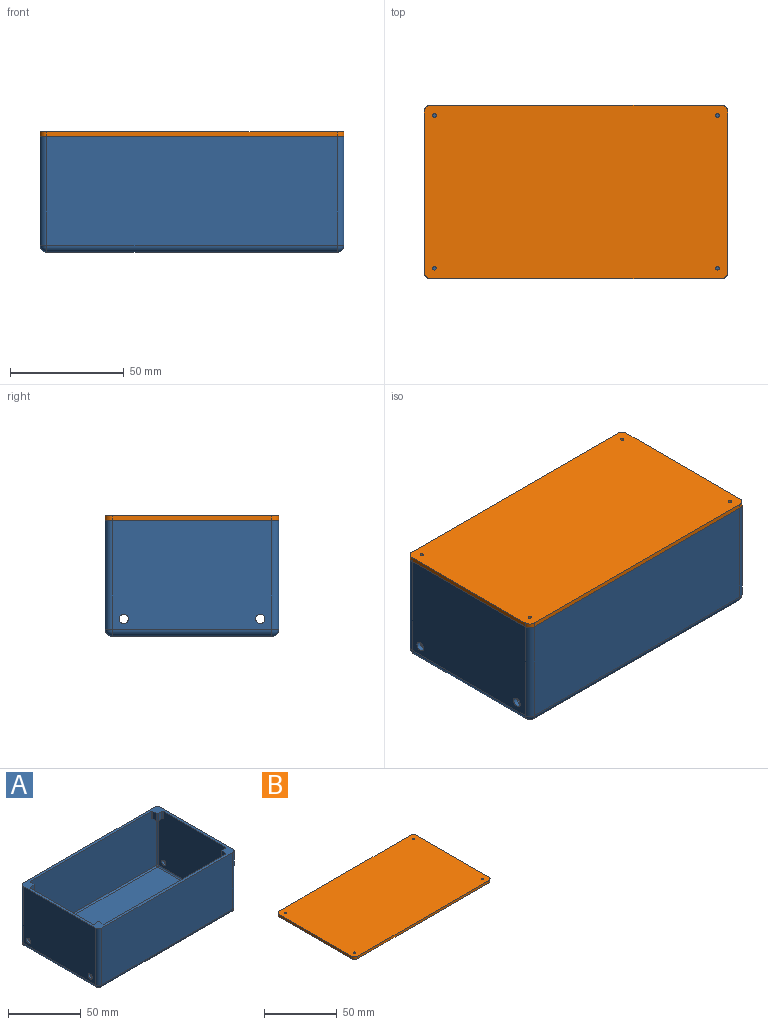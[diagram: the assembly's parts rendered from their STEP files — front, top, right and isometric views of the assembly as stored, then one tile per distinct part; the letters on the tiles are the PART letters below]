
ASSEMBLY  parts=2 mates=1
PART A: 63 faces, bbox 133.4x76.2x50.8 mm
  f0: plane 70.1x47.75mm, normal (1,0,0), area 3260.4mm2, adj f4,f23,f27,f33,f43,f46,f49,f50
  f1: plane 127.25x47.75mm, normal (0,1,0), area 6015.3mm2, adj f4,f24,f27,f29,f37,f46,f56,f62
  f2: plane 127.25x47.75mm, normal (0,-1,0), area 6015.3mm2, adj f4,f25,f31,f33,f40,f43,f58,f60
  f3: plane 70.1x47.75mm, normal (-1,0,0), area 3260.4mm2, adj f4,f26,f29,f31,f37,f40,f47,f48
  f4: plane 133.35x76.2mm, normal (0,0,1), area 930.8mm2, adj f0,f1,f2,f3,f5,f6,f7,f8
  f5: plane 70.1x47.75mm, normal (-1,0,0), area 3321.7mm2, adj f4,f10,f14,f20,f49,f50
  f6: plane 127.25x47.75mm, normal (0,-1,0), area 6076.6mm2, adj f4,f11,f14,f16
  f7: plane 70.1x47.75mm, normal (1,0,0), area 3321.7mm2, adj f4,f13,f16,f18,f47,f48
  f8: plane 127.25x47.75mm, normal (0,1,0), area 6076.6mm2, adj f4,f12,f18,f20
  f9: plane 127.25x70.1mm, normal (0,0,-1), area 8921mm2, adj f10,f11,f12,f13
  f10: cylinder r=3.05mm len=70.1mm, axis (0,-1,0), area 335.6mm2, adj f5,f9,f15,f21
  f11: cylinder r=3.05mm len=127.25mm, axis (1,0,0), area 609.3mm2, adj f6,f9,f15,f17
  f12: cylinder r=3.05mm len=127.25mm, axis (-1,0,0), area 609.3mm2, adj f8,f9,f19,f21
  f13: cylinder r=3.05mm len=70.1mm, axis (0,1,0), area 335.6mm2, adj f7,f9,f17,f19
  f14: cylinder r=3.05mm len=47.75mm, axis (0,0,1), area 228.6mm2, adj f4,f5,f6,f15
  f15: sphere r=3.05mm, area 14.6mm2, adj f10,f11,f14
  f16: cylinder r=3.05mm len=47.75mm, axis (0,0,-1), area 228.6mm2, adj f4,f6,f7,f17
  f17: sphere r=3.05mm, area 14.6mm2, adj f11,f13,f16
  f18: cylinder r=3.05mm len=47.75mm, axis (0,0,1), area 228.6mm2, adj f4,f7,f8,f19
  f19: sphere r=3.05mm, area 14.6mm2, adj f12,f13,f18
  f20: cylinder r=3.05mm len=47.75mm, axis (0,0,-1), area 228.6mm2, adj f4,f5,f8,f21
  f21: sphere r=3.05mm, area 14.6mm2, adj f10,f12,f20
  f22: plane 127.25x70.1mm, normal (0,0,1), area 8921mm2, adj f23,f24,f25,f26
  f23: cylinder r=1.02mm len=70.1mm, axis (0,-1,0), area 111.9mm2, adj f0,f22,f28,f34
  f24: cylinder r=1.02mm len=127.25mm, axis (1,0,0), area 203.1mm2, adj f1,f22,f28,f30
  f25: cylinder r=1.02mm len=127.25mm, axis (-1,0,0), area 203.1mm2, adj f2,f22,f32,f34
  f26: cylinder r=1.02mm len=70.1mm, axis (0,1,0), area 111.9mm2, adj f3,f22,f30,f32
  f27: cylinder r=1.02mm len=41.4mm, axis (0,0,1), area 66.1mm2, adj f0,f1,f28,f46
  f28: sphere r=1.02mm, area 1.6mm2, adj f23,f24,f27
  f29: cylinder r=1.02mm len=41.4mm, axis (0,0,-1), area 66.1mm2, adj f1,f3,f30,f37
  f30: sphere r=1.02mm, area 1.6mm2, adj f24,f26,f29
  f31: cylinder r=1.02mm len=41.4mm, axis (0,0,1), area 66.1mm2, adj f2,f3,f32,f40
  f32: sphere r=1.02mm, area 1.6mm2, adj f25,f26,f31
  f33: cylinder r=1.02mm len=41.4mm, axis (0,0,-1), area 66.1mm2, adj f0,f2,f34,f43
  f34: sphere r=1.02mm, area 1.6mm2, adj f23,f25,f33
  f35: plane 6.35x3.56mm, normal (0,1,0), area 22.6mm2, adj f4,f37,f54,f61
  f36: plane 6.35x3.56mm, normal (-1,0,0), area 22.6mm2, adj f4,f37,f54,f62
  f37: plane 5.84x5.84mm, normal (0,0,-1), area 25.7mm2, adj f1,f3,f29,f35,f36,f54,f61,f62
  f38: plane 6.35x3.56mm, normal (-1,0,0), area 22.6mm2, adj f4,f40,f53,f60
  f39: plane 6.35x3.56mm, normal (0,-1,0), area 22.6mm2, adj f4,f40,f53,f59
  f40: plane 5.84x5.84mm, normal (0,0,-1), area 25.7mm2, adj f2,f3,f31,f38,f39,f53,f59,f60
  f41: plane 6.35x3.56mm, normal (0,-1,0), area 22.6mm2, adj f4,f43,f52,f57
  f42: plane 6.35x3.56mm, normal (1,0,0), area 22.6mm2, adj f4,f43,f52,f58
  f43: plane 5.84x5.84mm, normal (0,0,-1), area 25.7mm2, adj f0,f2,f33,f41,f42,f52,f57,f58
  f44: plane 6.35x3.56mm, normal (1,0,0), area 22.6mm2, adj f4,f46,f51,f56
  f45: plane 6.35x3.56mm, normal (0,1,0), area 22.6mm2, adj f4,f46,f51,f55
  f46: plane 5.84x5.84mm, normal (0,0,-1), area 25.7mm2, adj f0,f1,f27,f44,f45,f51,f55,f56
  f47: cylinder r=2.03mm len=4.06mm, axis (-1,0,0), area 25.9mm2, adj f3,f7
  f48: cylinder r=2.03mm len=4.06mm, axis (-1,0,0), area 25.9mm2, adj f3,f7
  f49: cylinder r=2.03mm len=4.06mm, axis (-1,0,0), area 25.9mm2, adj f0,f5
  f50: cylinder r=2.03mm len=4.06mm, axis (-1,0,0), area 25.9mm2, adj f0,f5
  f51: cylinder r=0.76mm len=6.35mm, axis (0,0,-1), area 7.6mm2, adj f4,f44,f45,f46
  f52: cylinder r=0.76mm len=6.35mm, axis (0,0,-1), area 7.6mm2, adj f4,f41,f42,f43
  f53: cylinder r=0.76mm len=6.35mm, axis (0,0,-1), area 7.6mm2, adj f4,f38,f39,f40
  f54: cylinder r=0.76mm len=6.35mm, axis (0,0,-1), area 7.6mm2, adj f4,f35,f36,f37
  f55: cylinder r=0.76mm len=6.35mm, axis (0,0,1), area 7.6mm2, adj f0,f4,f45,f46
  f56: cylinder r=0.76mm len=6.35mm, axis (0,0,1), area 7.6mm2, adj f1,f4,f44,f46
  f57: cylinder r=0.76mm len=6.35mm, axis (0,0,-1), area 7.6mm2, adj f0,f4,f41,f43
  f58: cylinder r=0.76mm len=6.35mm, axis (0,0,1), area 7.6mm2, adj f2,f4,f42,f43
  f59: cylinder r=0.76mm len=6.35mm, axis (0,0,-1), area 7.6mm2, adj f3,f4,f39,f40
  f60: cylinder r=0.76mm len=6.35mm, axis (0,0,-1), area 7.6mm2, adj f2,f4,f38,f40
  f61: cylinder r=0.76mm len=6.35mm, axis (0,0,1), area 7.6mm2, adj f3,f4,f35,f37
  f62: cylinder r=0.76mm len=6.35mm, axis (0,0,-1), area 7.6mm2, adj f1,f4,f36,f37
PART B: 14 faces, bbox 133.4x76.2x2 mm
  f0: plane 70.1x2.03mm, normal (-1,0,0), area 142.5mm2, adj f4,f5,f6,f9
  f1: plane 127.25x2.03mm, normal (0,-1,0), area 258.6mm2, adj f4,f5,f6,f7
  f2: plane 70.1x2.03mm, normal (1,0,0), area 142.5mm2, adj f4,f5,f7,f8
  f3: plane 127.25x2.03mm, normal (0,1,0), area 258.6mm2, adj f4,f5,f8,f9
  f4: plane 133.35x76.2mm, normal (0,0,1), area 10146mm2, adj f0,f1,f2,f3,f6,f7,f8,f9
  f5: plane 133.35x76.2mm, normal (0,0,-1), area 10146mm2, adj f0,f1,f2,f3,f6,f7,f8,f9
  f6: cylinder r=3.05mm len=3.05mm, axis (0,0,1), area 9.7mm2, adj f0,f1,f4,f5
  f7: cylinder r=3.05mm len=3.05mm, axis (0,0,-1), area 9.7mm2, adj f1,f2,f4,f5
  f8: cylinder r=3.05mm len=3.05mm, axis (0,0,1), area 9.7mm2, adj f2,f3,f4,f5
  f9: cylinder r=3.05mm len=3.05mm, axis (0,0,-1), area 9.7mm2, adj f0,f3,f4,f5
  f10: cylinder r=0.76mm len=2.03mm, axis (0,0,1), area 9.7mm2, adj f4,f5
  f11: cylinder r=0.76mm len=2.03mm, axis (0,0,1), area 9.7mm2, adj f4,f5
  f12: cylinder r=0.76mm len=2.03mm, axis (0,0,1), area 9.7mm2, adj f4,f5
  f13: cylinder r=0.76mm len=2.03mm, axis (0,0,1), area 9.7mm2, adj f4,f5
PLACE A t=(-39.36,-13.58,-12.28)mm
PLACE B t=(-39.37,-13.57,38.52)mm
MATE planar B.f5 <-> A.f4  axis (0,0,-1) through (27.31,24.53,38.52)mm
